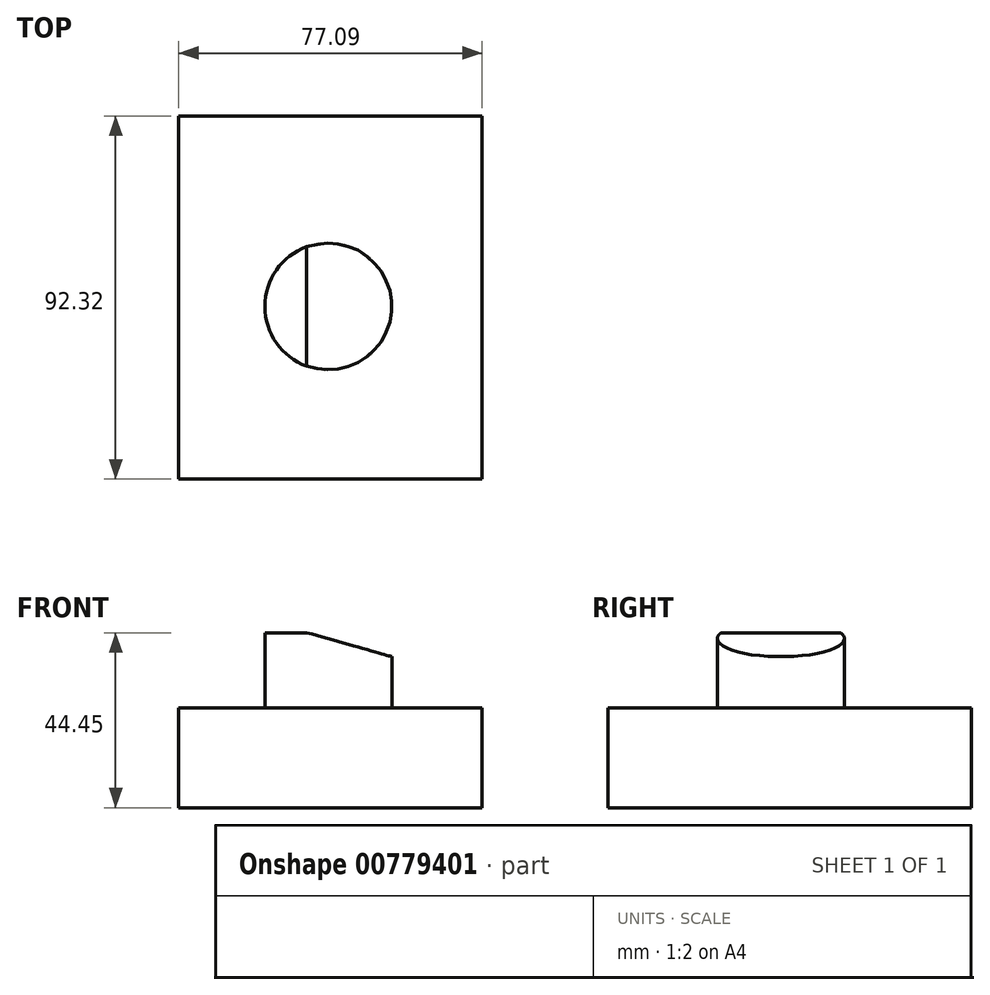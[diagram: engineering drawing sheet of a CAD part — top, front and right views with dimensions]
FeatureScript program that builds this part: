
annotation { "Feature Type Name" : "Feature", "Feature Type Description" : "" }
export const myFeature = defineFeature(function(context is Context, id is Id, definition is map)
    precondition{}
    {
        {
            var Q0;
            Q0=qCreatedBy(makeId("Top.planeOp"),FACE);
            var sketch = newSketch(context, id + "F0", { "sketchPlane" : qUnion([Q0])});
            skLineSegment(sketch, "E0.bottom", {"start": v(-38.06, 48.43) * mm, "end": v(39.03, 48.43) * mm});
            skLineSegment(sketch, "E0.top", {"start": v(-38.06, -43.9) * mm, "end": v(39.03, -43.9) * mm});
            skLineSegment(sketch, "E0.left", {"start": v(-38.06, 48.43) * mm, "end": v(-38.06, -43.9) * mm});
            skLineSegment(sketch, "E0.right", {"start": v(39.03, 48.43) * mm, "end": v(39.03, -43.9) * mm});
            skSolve(sketch);
        }
        {
            var Q0;
            Q0 = qSketchRegion(id + "F0", true);
            extrude(context, id + "F1", {"entities" : qUnion([Q0]), "depth" : 25.4 * mm, "offsetDistance" : 25.4 * mm});
        }
        {
            var Q0;
            Q0=qCreatedBy(makeId("Top.planeOp"),FACE);
            var sketch = newSketch(context, id + "F2", { "sketchPlane" : qUnion([Q0])});
            skCircle(sketch, "E1", {"center": v(0, 0) * mm, "radius": 16.17 * mm});
            skSolve(sketch);
        }
        {
            var Q0;
            Q0 = qSketchRegion(id + "F2", true);
            extrude(context, id + "F3", {"entities" : qUnion([Q0]), "operationType" : NewBodyOperationType.ADD, "depth" : 44.45 * mm, "offsetDistance" : 25.4 * mm});
        }
        {
            var Q0;
            Q0=qCreatedBy(makeId("Front.planeOp"),FACE);
            var sketch = newSketch(context, id + "F4", { "sketchPlane" : qUnion([Q0])});
            skLineSegment(sketch, "E2", {"start": v(-43.9, 55.23) * mm, "end": v(47.13, 29.64) * mm});
            skLineSegment(sketch, "E3", {"start": v(47.13, 29.64) * mm, "end": v(39.68, 63) * mm});
            skLineSegment(sketch, "E4", {"start": v(39.68, 63) * mm, "end": v(-43.9, 55.23) * mm});
            skSolve(sketch);
        }
        {
            var Q0;
            Q0 = qSketchRegion(id + "F4", true);
            extrude(context, id + "F5", {"entities" : qUnion([Q0]), "operationType" : NewBodyOperationType.REMOVE, "endBound" : BoundingType.SYMMETRIC, "depth" : 228.6 * mm, "offsetDistance" : 25.4 * mm});
        }
    });
